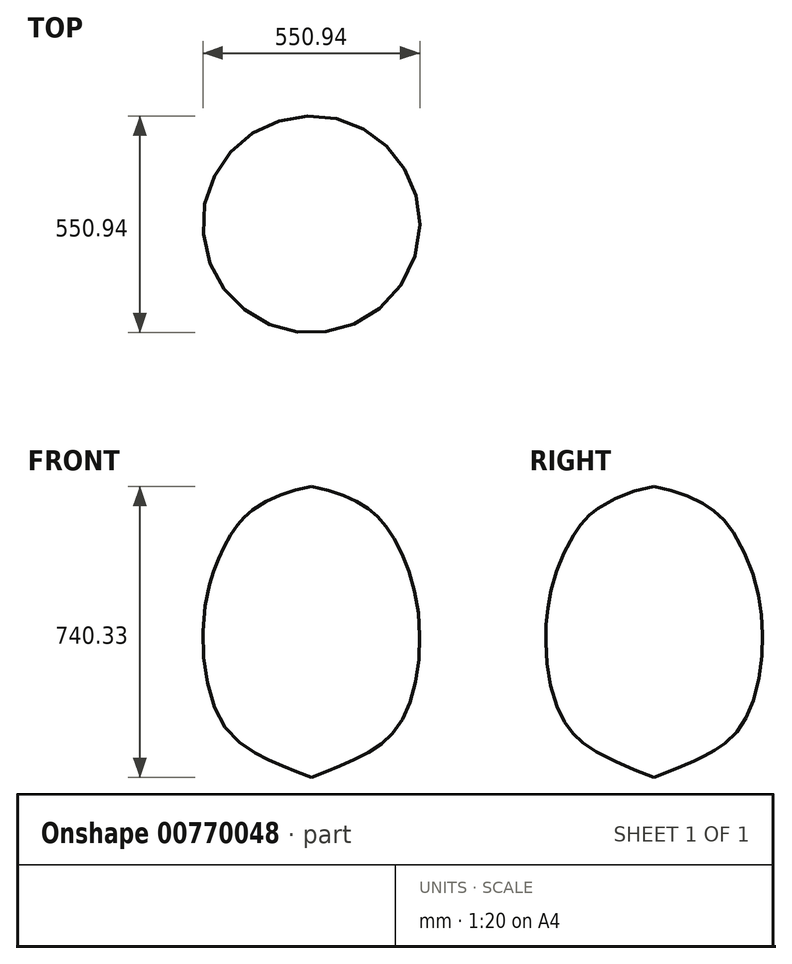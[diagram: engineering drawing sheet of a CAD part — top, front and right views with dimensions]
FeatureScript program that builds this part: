
annotation { "Feature Type Name" : "Feature", "Feature Type Description" : "" }
export const myFeature = defineFeature(function(context is Context, id is Id, definition is map)
    precondition{}
    {
        {
            var Q0;
            Q0=qCreatedBy(makeId("Front.planeOp"),FACE);
            var sketch = newSketch(context, id + "F0", { "sketchPlane" : qUnion([Q0])});
            skFitSpline(sketch, "E0", {"points": [v(0, 0) * mm, v(131.35, 56.48) * mm, v(235.17, 154.7) * mm, v(271.06, 425.93) * mm, v(200.5, 623.52) * mm, v(131.55, 691.91) * mm, v(0, 740.33) * mm], "startDerivative": vector(813.32, 331.86) * mm, "endDerivative": vector(-1044.4, 213.67) * mm});
            skLineSegment(sketch, "E1", {"start": v(0, 0) * mm, "end": v(0, 740.33) * mm});
            skSolve(sketch);
        }
        {
            var Q0;
            Q0=makeQuery(id+"F0.imprint","IMPRINT",FACE,{"disambiguationData":[TD([[makeQuery(id+"F0.imprint","IMPRINT",EDGE,{"derivedFrom":sQuery(id+"F0.wireOp",EDGE,"E0")}),1.0]])]});
            var Q1;
            Q1=sQuery(id+"F0.wireOp",EDGE,"E1");
            revolve(context, id + "F1", {"surfaceOperationType" : NewSurfaceOperationType.NEW, "entities" : qUnion([Q0]), "axis" : qUnion([Q1]), "revolveType" : RevolveType.FULL});
        }
    });
